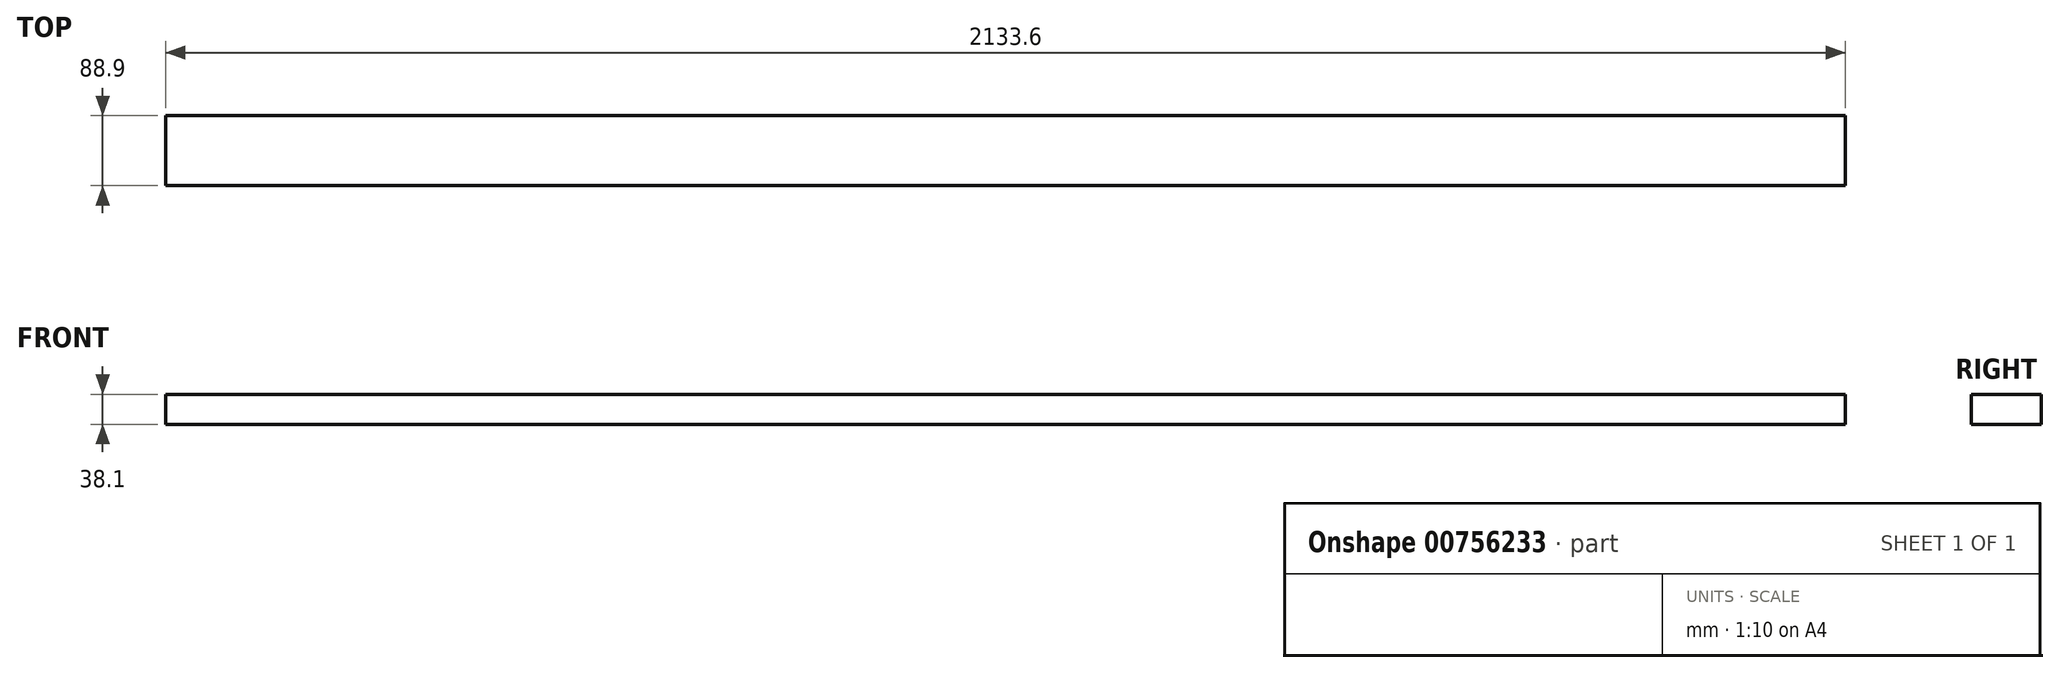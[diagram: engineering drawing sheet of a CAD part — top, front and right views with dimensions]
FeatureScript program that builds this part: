
annotation { "Feature Type Name" : "Feature", "Feature Type Description" : "" }
export const myFeature = defineFeature(function(context is Context, id is Id, definition is map)
    precondition{}
    {
        {
            var Q0;
            Q0=qCreatedBy(makeId("Front.planeOp"),FACE);
            var sketch = newSketch(context, id + "F0", { "sketchPlane" : qUnion([Q0])});
            skLineSegment(sketch, "E0.bottom", {"start": v(-1066.8, 19.05) * mm, "end": v(1066.8, 19.05) * mm});
            skLineSegment(sketch, "E0.top", {"start": v(-1066.8, -19.05) * mm, "end": v(1066.8, -19.05) * mm});
            skLineSegment(sketch, "E0.left", {"start": v(-1066.8, 19.05) * mm, "end": v(-1066.8, -19.05) * mm});
            skLineSegment(sketch, "E0.right", {"start": v(1066.8, 19.05) * mm, "end": v(1066.8, -19.05) * mm});
            skPoint(sketch, "E0.middle", {"position": v(0, 0) * mm});
            skSolve(sketch);
        }
        {
            var Q0;
            Q0=makeQuery(id+"F0.imprint","IMPRINT",FACE,{"disambiguationData":[TD([[makeQuery(id+"F0.imprint","IMPRINT",EDGE,{"derivedFrom":sQuery(id+"F0.wireOp",EDGE,"E0.bottom")}),-1.0]])]});
            extrude(context, id + "F1", {"entities" : qUnion([Q0]), "endBound" : BoundingType.SYMMETRIC, "depth" : 88.9 * mm, "offsetDistance" : 25.4 * mm});
        }
    });
